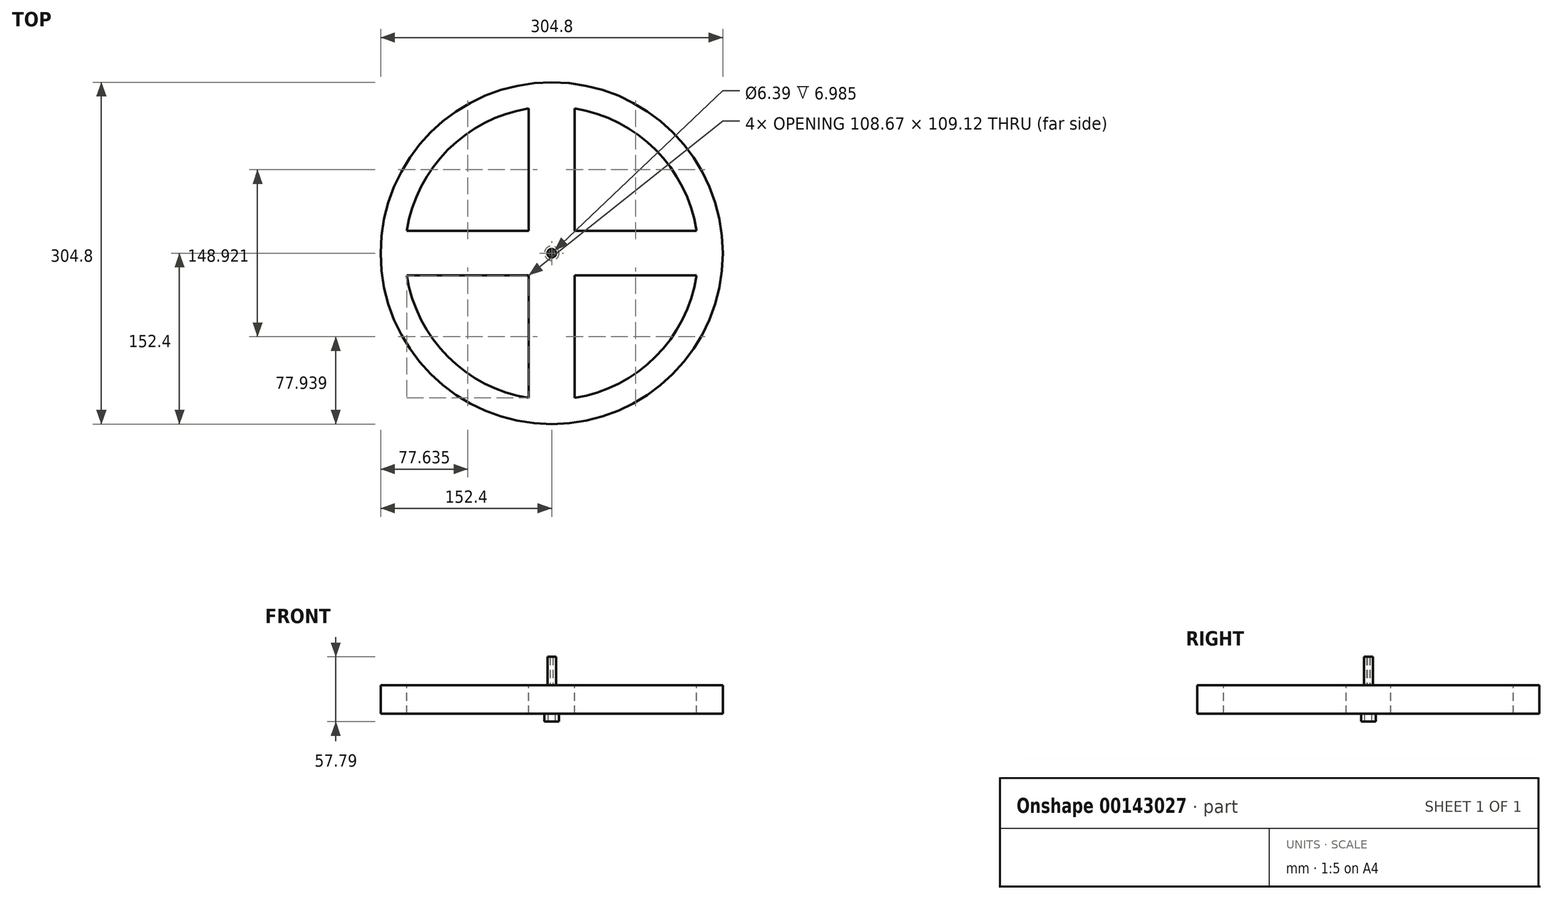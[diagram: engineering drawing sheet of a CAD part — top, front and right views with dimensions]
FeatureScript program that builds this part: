
annotation { "Feature Type Name" : "Feature", "Feature Type Description" : "" }
export const myFeature = defineFeature(function(context is Context, id is Id, definition is map)
    precondition{}
    {
        {
            var Q0;
            Q0=qCreatedBy(makeId("Top.planeOp"),FACE);
            var sketch = newSketch(context, id + "F0", { "sketchPlane" : qUnion([Q0])});
            skCircle(sketch, "E0", {"center": v(0, 0) * mm, "radius": 152.4 * mm});
            skSolve(sketch);
        }
        {
            var Q0;
            Q0 = qSketchRegion(id + "F0", true);
            extrude(context, id + "F1", {"entities" : qUnion([Q0]), "depth" : 12.7 * mm, "hasSecondDirection" : true, "secondDirectionOppositeDirection" : true, "secondDirectionDepth" : 12.7 * mm});
        }
        {
            var Q0;
            Q0=makeQuery(id+"F1.opExtrude","CAP_FACE",FACE,{"disambiguationData":[OSD([sQuery(id+"F0.wireOp",EDGE,"E0")])],"isStart":false});
            var sketch = newSketch(context, id + "F2", { "sketchPlane" : qUnion([Q0])});
            skCircle(sketch, "E1", {"center": v(0, 0) * mm, "radius": 3.86 * mm});
            skCircle(sketch, "E2", {"center": v(0, 0) * mm, "radius": 1.59 * mm});
            skSolve(sketch);
        }
        {
            var Q0;
            Q0 = qSketchRegion(id + "F2", true);
            extrude(context, id + "F3", {"entities" : qUnion([Q0]), "operationType" : NewBodyOperationType.ADD, "depth" : 25.4 * mm});
        }
        {
            var Q0;
            {var subQ0=sQuery(id+"F0.wireOp",EDGE,"E0");Q0=makeQuery(id+"F3.boolean.opBoolean","SPLIT",FACE,{"disambiguationData":[TD([makeQuery(id+"F1.opExtrude","SWEPT_FACE",FACE,{"disambiguationData":[OSD([subQ0])]})])],"derivedFrom":makeQuery(id+"F1.opExtrude","CAP_FACE",FACE,{"disambiguationData":[OSD([subQ0])],"isStart":false})});}
            var sketch = newSketch(context, id + "F4", { "sketchPlane" : qUnion([Q0])});
            skArc(sketch, "E3", {"start": v(-129.1, -19.9) * mm, "mid": v(-92.56, -92.18) * mm, "end": v(-20.43, -129.02) * mm});
            skLineSegment(sketch, "E4", {"start": v(-129.1, -19.9) * mm, "end": v(-20.43, -19.9) * mm});
            skLineSegment(sketch, "E5", {"start": v(-20.43, -19.9) * mm, "end": v(-20.43, -129.02) * mm});
            skLineSegment(sketch, "E6.MirrorCS", {"start": v(-20.43, 19.9) * mm, "end": v(-20.43, 129.02) * mm});
            skLineSegment(sketch, "E7.MirrorCS", {"start": v(-129.1, 19.9) * mm, "end": v(-20.43, 19.9) * mm});
            skArc(sketch, "E8.MirrorCS", {"start": v(-129.1, 19.9) * mm, "mid": v(-92.56, 92.18) * mm, "end": v(-20.43, 129.02) * mm});
            skLineSegment(sketch, "E9.MirrorCS", {"start": v(20.43, 19.9) * mm, "end": v(20.43, 129.02) * mm});
            skArc(sketch, "E10.MirrorCS", {"start": v(129.1, 19.9) * mm, "mid": v(92.56, 92.18) * mm, "end": v(20.43, 129.02) * mm});
            skLineSegment(sketch, "E11.MirrorCS", {"start": v(129.1, 19.9) * mm, "end": v(20.43, 19.9) * mm});
            skLineSegment(sketch, "E12.MirrorCS", {"start": v(129.1, -19.9) * mm, "end": v(20.43, -19.9) * mm});
            skArc(sketch, "E13.MirrorCS", {"start": v(129.1, -19.9) * mm, "mid": v(92.56, -92.18) * mm, "end": v(20.43, -129.02) * mm});
            skLineSegment(sketch, "E14.MirrorCS", {"start": v(20.43, -19.9) * mm, "end": v(20.43, -129.02) * mm});
            skSolve(sketch);
        }
        {
            var Q0;
            Q0 = qSketchRegion(id + "F4", true);
            extrude(context, id + "F5", {"entities" : qUnion([Q0]), "operationType" : NewBodyOperationType.REMOVE, "endBound" : BoundingType.THROUGH_ALL, "oppositeDirection" : true, "depth" : 25.4 * mm});
        }
        {
            var Q0;
            Q0=makeQuery(id+"F2.imprint","IMPRINT",FACE,{"disambiguationData":[TD([[makeQuery(id+"F2.imprint","IMPRINT",EDGE,{"derivedFrom":sQuery(id+"F2.wireOp",EDGE,"E1")}),-1.0]])]});
            var sketch = newSketch(context, id + "F6", { "sketchPlane" : qUnion([Q0])});
            skLineSegment(sketch, "E15.bottom", {"start": v(1.05, 2.33) * mm, "end": v(1.94, 2.33) * mm});
            skLineSegment(sketch, "E15.top", {"start": v(1.05, -2.82) * mm, "end": v(1.94, -2.82) * mm});
            skLineSegment(sketch, "E15.left", {"start": v(1.94, 2.33) * mm, "end": v(1.94, -2.82) * mm});
            skLineSegment(sketch, "E15.right", {"start": v(1.05, 2.33) * mm, "end": v(1.05, -2.82) * mm});
            skSolve(sketch);
        }
        {
            var Q0;
            Q0 = qSketchRegion(id + "F6", true);
            extrude(context, id + "F7", {"entities" : qUnion([Q0]), "operationType" : NewBodyOperationType.ADD, "depth" : 25.4 * mm});
        }
        {
            var Q0;
            Q0=makeQuery(id+"F1.opExtrude","CAP_FACE",FACE,{"disambiguationData":[OSD([sQuery(id+"F0.wireOp",EDGE,"E0")])],"isStart":true});
            var sketch = newSketch(context, id + "F8", { "sketchPlane" : qUnion([Q0])});
            skCircle(sketch, "E16", {"center": v(0, 0) * mm, "radius": 6.46 * mm});
            skCircle(sketch, "E17", {"center": v(0, 0) * mm, "radius": 3.2 * mm});
            skSolve(sketch);
        }
        {
            var Q0;
            Q0 = qSketchRegion(id + "F8", true);
            extrude(context, id + "F9", {"entities" : qUnion([Q0]), "operationType" : NewBodyOperationType.ADD, "depth" : 6.98 * mm});
        }
    });
